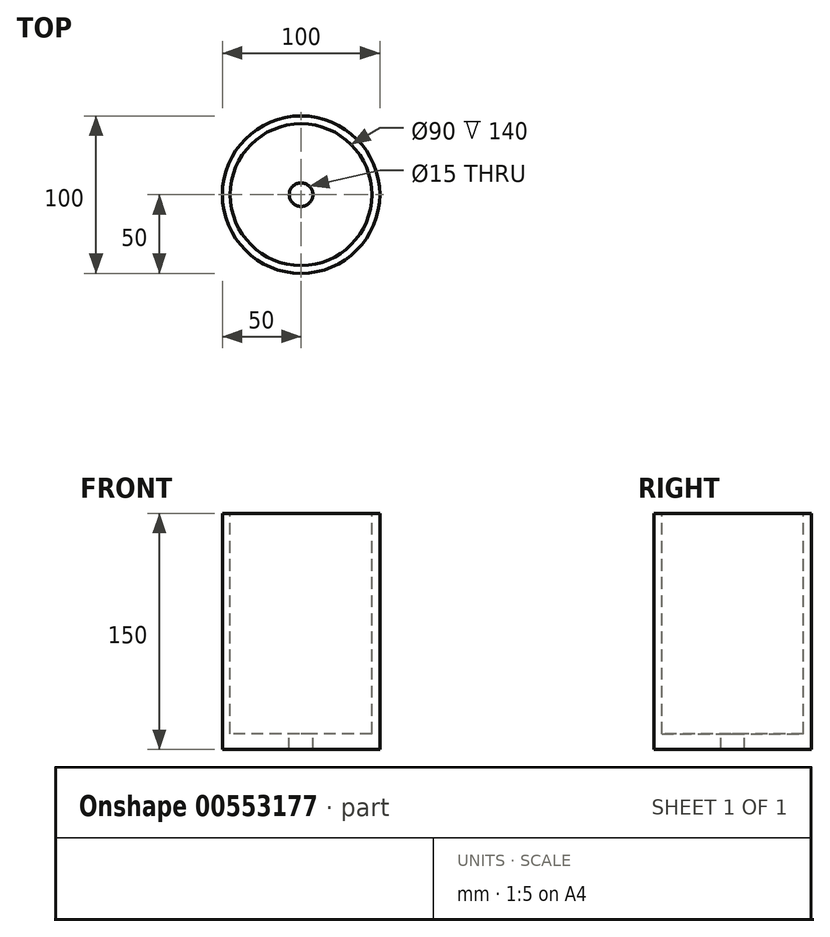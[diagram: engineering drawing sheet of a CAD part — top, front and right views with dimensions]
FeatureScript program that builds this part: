
annotation { "Feature Type Name" : "Feature", "Feature Type Description" : "" }
export const myFeature = defineFeature(function(context is Context, id is Id, definition is map)
    precondition{}
    {
        {
            var Q0;
            Q0=qCreatedBy(makeId("Top.planeOp"),FACE);
            var sketch = newSketch(context, id + "F0", { "sketchPlane" : qUnion([Q0])});
            skCircle(sketch, "E0", {"center": v(0, 0) * mm, "radius": 50 * mm});
            skSolve(sketch);
        }
        {
            var Q0;
            Q0=makeQuery(id+"F0.imprint","IMPRINT",FACE,{"disambiguationData":[TD([[makeQuery(id+"F0.imprint","IMPRINT",EDGE,{"derivedFrom":sQuery(id+"F0.wireOp",EDGE,"E0")}),1.0]])]});
            extrude(context, id + "F1", {"entities" : qUnion([Q0]), "depth" : 150 * mm, "offsetDistance" : 25 * mm});
        }
        {
            var Q0;
            Q0=makeQuery(id+"F1.opExtrude","CAP_FACE",FACE,{"disambiguationData":[OSD([sQuery(id+"F0.wireOp",EDGE,"E0")])],"isStart":false});
            var sketch = newSketch(context, id + "F2", { "sketchPlane" : qUnion([Q0])});
            skCircle(sketch, "E1", {"center": v(0, 0) * mm, "radius": 45 * mm});
            skSolve(sketch);
        }
        {
            var Q0;
            Q0=makeQuery(id+"F2.imprint","IMPRINT",FACE,{"disambiguationData":[TD([[makeQuery(id+"F2.imprint","IMPRINT",EDGE,{"derivedFrom":sQuery(id+"F2.wireOp",EDGE,"E1")}),1.0]])]});
            extrude(context, id + "F3", {"entities" : qUnion([Q0]), "operationType" : NewBodyOperationType.REMOVE, "oppositeDirection" : true, "depth" : 140 * mm, "offsetDistance" : 25 * mm});
        }
        {
            var Q0;
            Q0=makeQuery(id+"F3.boolean.opBoolean","COPY",FACE,{"derivedFrom":makeQuery(id+"F3.opExtrude","CAP_FACE",FACE,{"disambiguationData":[OSD([sQuery(id+"F2.wireOp",EDGE,"E1")])],"isStart":false})});
            var sketch = newSketch(context, id + "F4", { "sketchPlane" : qUnion([Q0])});
            skCircle(sketch, "E2", {"center": v(0, 0) * mm, "radius": 7.5 * mm});
            skSolve(sketch);
        }
        {
            var Q0;
            Q0 = qSketchRegion(id + "F4", true);
            extrude(context, id + "F5", {"entities" : qUnion([Q0]), "operationType" : NewBodyOperationType.REMOVE, "oppositeDirection" : true, "depth" : 20 * mm, "offsetDistance" : 25 * mm});
        }
    });
